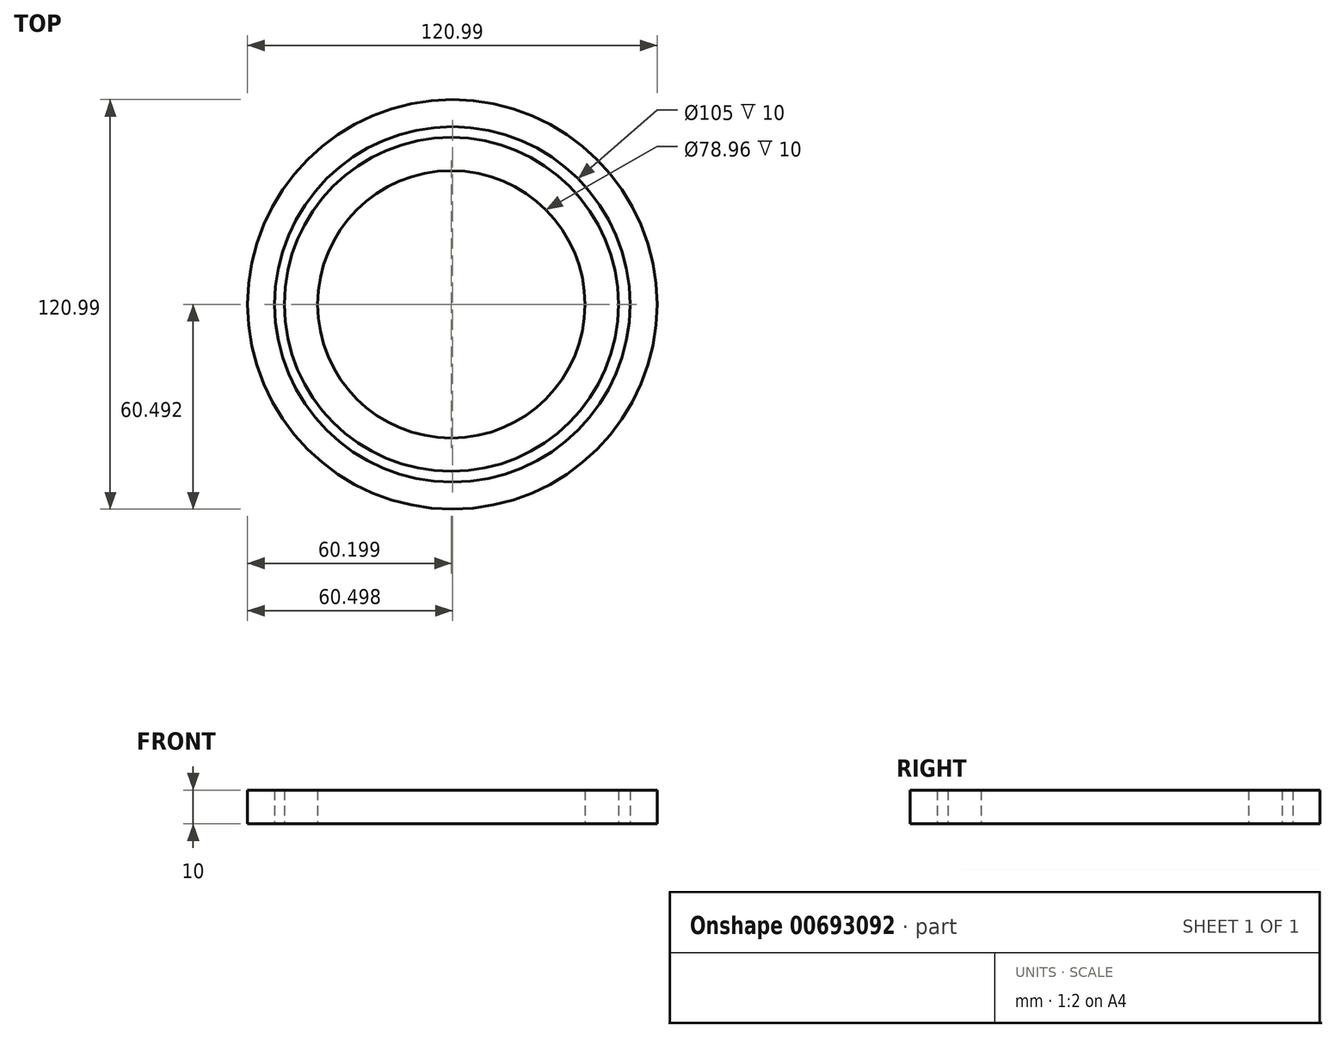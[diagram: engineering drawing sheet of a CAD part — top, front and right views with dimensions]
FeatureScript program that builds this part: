
annotation { "Feature Type Name" : "Feature", "Feature Type Description" : "" }
export const myFeature = defineFeature(function(context is Context, id is Id, definition is map)
    precondition{}
    {
        {
            var Q0;
            Q0=qCreatedBy(makeId("Top.planeOp"),FACE);
            var sketch = newSketch(context, id + "F0", { "sketchPlane" : qUnion([Q0])});
            skCircle(sketch, "E0", {"center": v(-113.67, 15.06) * mm, "radius": 52.5 * mm});
            skCircle(sketch, "E1", {"center": v(-113.67, 15.06) * mm, "radius": 60.5 * mm});
            skCircle(sketch, "E2", {"center": v(104.03, 15.06) * mm, "radius": 39.48 * mm});
            skCircle(sketch, "E3", {"center": v(104.03, 15.06) * mm, "radius": 49.34 * mm});
            skSolve(sketch);
        }
        {
            var Q0;
            Q0=makeQuery(id+"F0.imprint","IMPRINT",FACE,{"disambiguationData":[TD([[makeQuery(id+"F0.imprint","IMPRINT",EDGE,{"derivedFrom":sQuery(id+"F0.wireOp",EDGE,"E0")}),-1.0]])]});
            var Q1;
            Q1=makeQuery(id+"F0.imprint","IMPRINT",FACE,{"disambiguationData":[TD([[makeQuery(id+"F0.imprint","IMPRINT",EDGE,{"derivedFrom":sQuery(id+"F0.wireOp",EDGE,"E2")}),-1.0]])]});
            extrude(context, id + "F1", {"entities" : qUnion([Q0, Q1]), "depth" : 10 * mm, "offsetDistance" : 25 * mm});
        }
        {
            var Q0;
            Q0=makeQuery(id+"F1.opExtrude","SWEPT_BODY",BODY,{"disambiguationData":[OSD([sQuery(id+"F0.wireOp",EDGE,"E2"),sQuery(id+"F0.wireOp",EDGE,"E3")])]});
            transform(context, id + "F2", {"entities" : qUnion([Q0]), "transformType" : TransformType.TRANSLATION_3D, "dx" : -218 * mm, "dy" : 0 * mm, "dz" : 0 * mm, "makeCopy" : false});
        }
    });
